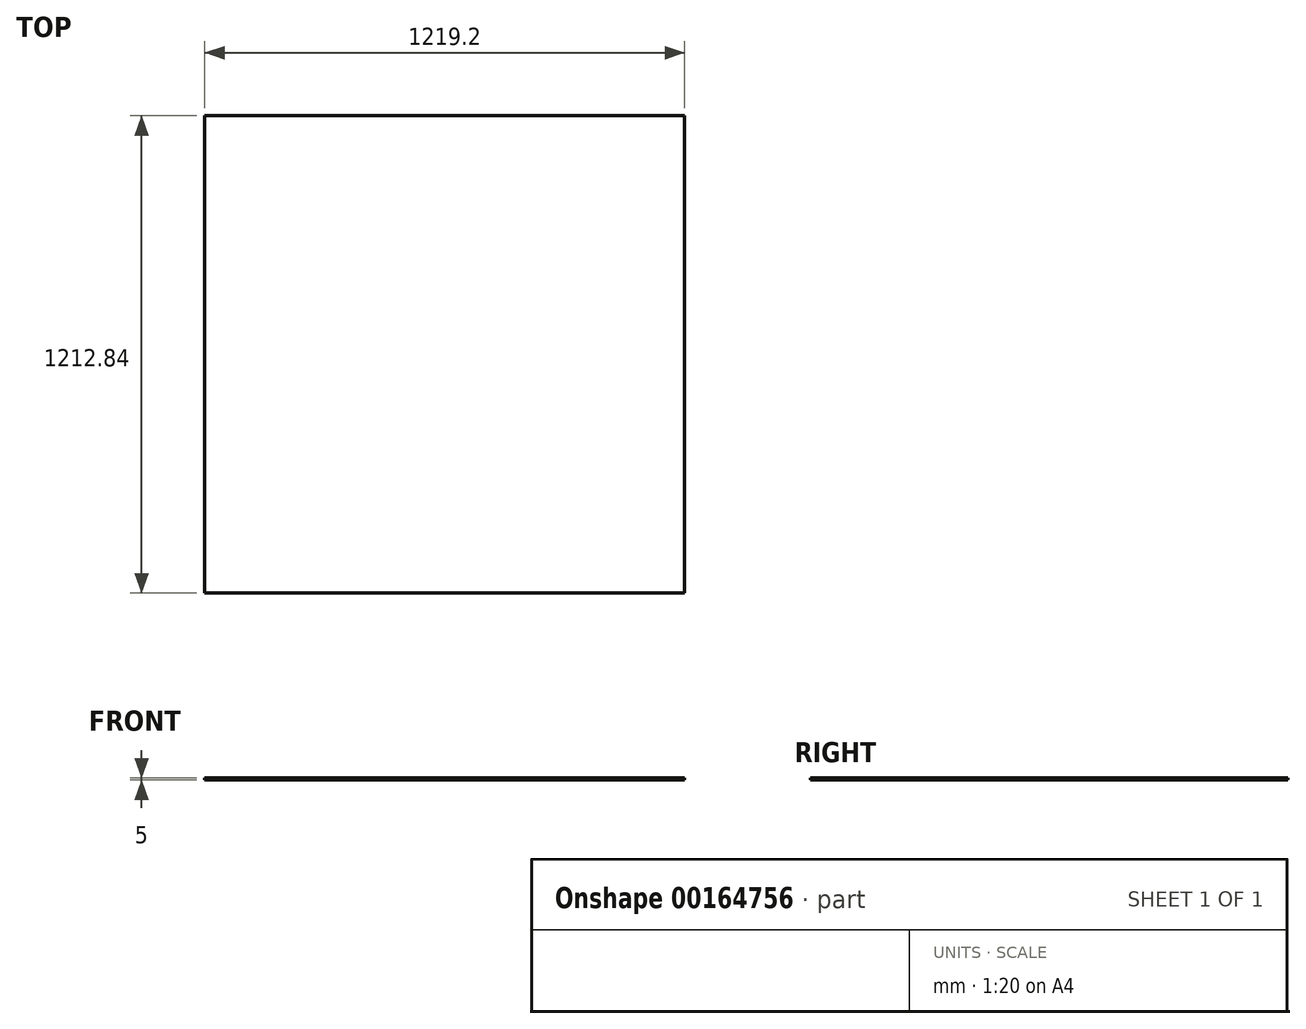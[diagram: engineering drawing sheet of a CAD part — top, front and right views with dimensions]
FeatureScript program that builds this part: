
annotation { "Feature Type Name" : "Feature", "Feature Type Description" : "" }
export const myFeature = defineFeature(function(context is Context, id is Id, definition is map)
    precondition{}
    {
        {
            var Q0;
            Q0=qCreatedBy(makeId("Top.planeOp"),FACE);
            var sketch = newSketch(context, id + "F0", { "sketchPlane" : qUnion([Q0])});
            skLineSegment(sketch, "E0.bottom", {"start": v(609.6, -606.43) * mm, "end": v(-609.6, -606.43) * mm});
            skLineSegment(sketch, "E0.top", {"start": v(609.6, 606.43) * mm, "end": v(-609.6, 606.43) * mm});
            skLineSegment(sketch, "E0.left", {"start": v(609.6, -606.43) * mm, "end": v(609.6, 606.43) * mm});
            skLineSegment(sketch, "E0.right", {"start": v(-609.6, -606.43) * mm, "end": v(-609.6, 606.43) * mm});
            skPoint(sketch, "E0.middle", {"position": v(0, 0) * mm});
            skSolve(sketch);
        }
        {
            var Q0;
            Q0 = qSketchRegion(id + "F0", true);
            extrude(context, id + "F1", {"entities" : qUnion([Q0]), "depth" : 5 * mm});
        }
    });
